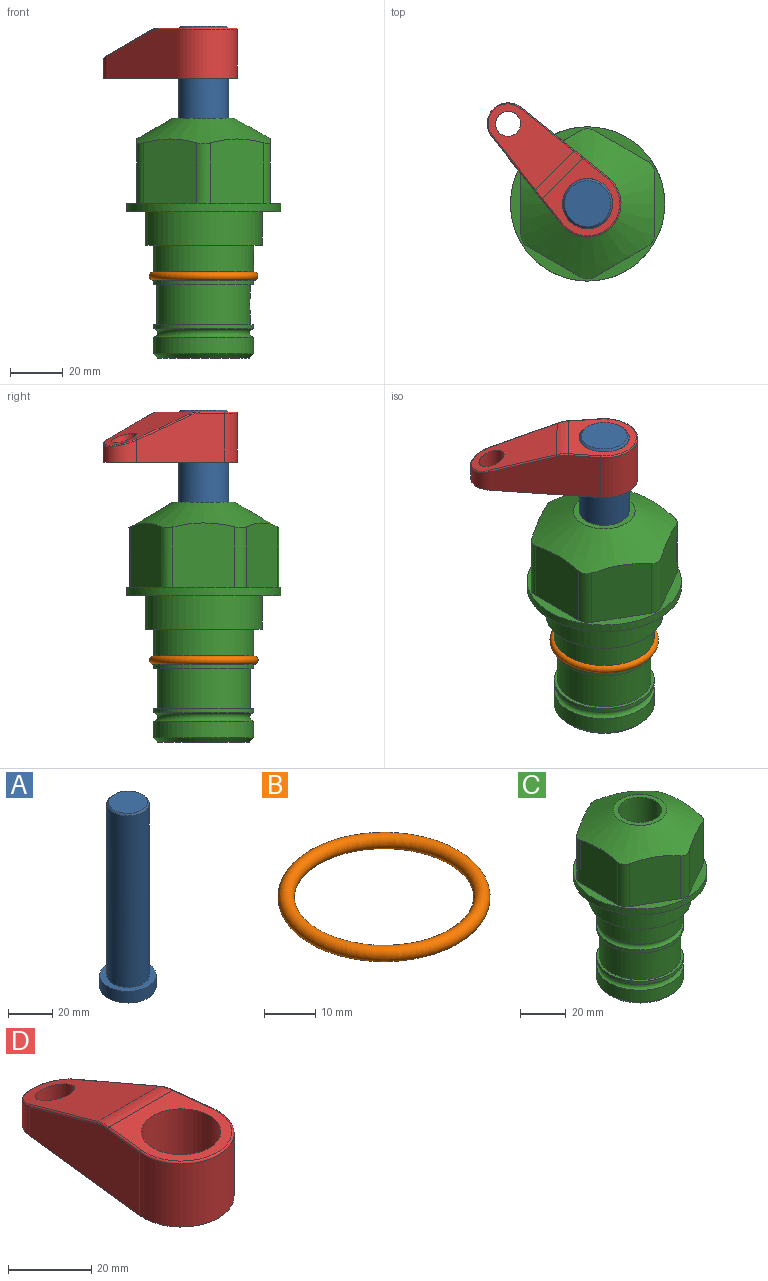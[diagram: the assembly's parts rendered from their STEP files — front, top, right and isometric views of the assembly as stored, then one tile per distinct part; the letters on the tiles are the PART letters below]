
ASSEMBLY  parts=4 mates=2
PART A: 6 faces, bbox 25.4x25.4x101.6 mm
  f0: plane 17.46x17.46mm, normal (0,0,1), area 239.5mm2, adj f5
  f1: plane 25.4x25.4mm, normal (0,0,-1), area 506.7mm2, adj f2
  f2: cylinder r=12.7mm len=25.4mm, axis (0,0,1), area 506.7mm2, adj f1,f3
  f3: plane 25.4x25.4mm, normal (0,0,1), area 221.7mm2, adj f2,f4
  f4: cylinder r=9.53mm len=94.46mm, axis (0,0,1), area 5653mm2, adj f3,f5
  f5: cone r=8.73mm half-angle=45deg, axis (0,0,-1), area 64.4mm2, adj f0,f4
PART B: 1 faces, bbox 44.7x44.7x3.2 mm
  f0: torus R=19.05mm, axis (0,0,1), area 1193.9mm2
PART C: 36 faces, bbox 58.7x58.7x91.2 mm
  f0: cylinder r=17.78mm len=35.56mm, axis (0,0,1), area 1670.8mm2, adj f23,f24,f31
  f1: cylinder r=19.05mm len=38.1mm, axis (0,0,1), area 1191.9mm2, adj f26,f27,f30
  f2: plane 58.66x58.66mm, normal (0,0,-1), area 1150.6mm2, adj f3,f28
  f3: cylinder r=29.33mm len=58.66mm, axis (0,0,-1), area 585.1mm2, adj f2,f4
  f4: plane 58.66x58.66mm, normal (0,0,1), area 475.9mm2, adj f3,f5,f6,f7,f8,f9,f10,f11
  f5: plane 24.5x20.32mm, normal (-0.5,0.87,0), area 562.8mm2, adj f4,f15,f16,f17
  f6: plane 24.5x20.32mm, normal (0.5,0.87,0), area 562.8mm2, adj f4,f14,f15,f17
  f7: plane 24.5x23.48mm, normal (1,0,0), area 562.8mm2, adj f4,f13,f14,f17
  f8: plane 24.5x20.32mm, normal (0.5,-0.87,0), area 562.8mm2, adj f4,f12,f13,f17
  f9: plane 24.5x20.32mm, normal (-0.5,-0.87,0), area 562.8mm2, adj f4,f11,f12,f17
  f10: plane 24.5x23.48mm, normal (-1,0,0), area 562.8mm2, adj f4,f11,f16,f17
  f11: cylinder r=5.08mm len=23.01mm, axis (0,0,-1), area 121.2mm2, adj f4,f9,f10,f17
  f12: cylinder r=5.08mm len=23.01mm, axis (0,0,-1), area 121.2mm2, adj f4,f8,f9,f17
  f13: cylinder r=5.08mm len=23.01mm, axis (0,0,-1), area 121.2mm2, adj f4,f7,f8,f17
  f14: cylinder r=5.08mm len=23.01mm, axis (0,0,-1), area 121.2mm2, adj f4,f6,f7,f17
  f15: cylinder r=5.08mm len=23.01mm, axis (0,0,-1), area 121.2mm2, adj f4,f5,f6,f17
  f16: cylinder r=5.08mm len=23.01mm, axis (0,0,-1), area 121.2mm2, adj f4,f5,f10,f17
  f17: cone r=11.73mm half-angle=60deg, axis (0,0,-1), area 2071.8mm2, adj f5,f6,f7,f8,f9,f10,f11,f12
  f18: plane 23.46x23.46mm, normal (0,0,1), area 147.4mm2, adj f17,f35
  f19: plane 34.93x34.93mm, normal (0,0,-1), area 958mm2, adj f29
  f20: cylinder r=19.05mm len=38.1mm, axis (0,0,1), area 760.1mm2, adj f21,f29
  f21: torus R=19.05mm, axis (0,0,1), area 565.3mm2, adj f20,f22
  f22: cylinder r=19.05mm len=38.1mm, axis (0,0,1), area 190mm2, adj f21,f23
  f23: plane 38.1x38.1mm, normal (0,0,1), area 146.9mm2, adj f0,f22
  f24: plane 38.1x38.1mm, normal (0,0,-1), area 146.9mm2, adj f0,f25
  f25: cylinder r=19.05mm len=38.1mm, axis (0,0,1), area 190mm2, adj f24,f26
  f26: torus R=19.05mm, axis (0,0,1), area 565.3mm2, adj f1,f25
  f27: plane 44.45x44.45mm, normal (0,0,-1), area 411.7mm2, adj f1,f28
  f28: cylinder r=22.23mm len=44.45mm, axis (0,0,1), area 1773.5mm2, adj f2,f27
  f29: cone r=19.05mm half-angle=45deg, axis (0,0,1), area 257.5mm2, adj f19,f20
  f30: cylinder r=3.17mm len=6.75mm, axis (-1,0,0), area 128mm2, adj f1,f33
  f31: cylinder r=3.17mm len=6.35mm, axis (-1,0,0), area 102.5mm2, adj f0,f33
  f32: plane 25.4x25.4mm, normal (0,0,1), area 506.7mm2, adj f33
  f33: cylinder r=12.7mm len=66.42mm, axis (0,0,-1), area 5236.2mm2, adj f30,f31,f32,f34
  f34: cone r=9.53mm half-angle=30deg, axis (0,0,-1), area 443.4mm2, adj f33,f35
  f35: cylinder r=9.53mm len=19.05mm, axis (0,0,-1), area 849mm2, adj f18,f34
PART D: 44 faces, bbox 27.5x64.5x19.1 mm
  f0: plane 2.3x0.95mm, normal (0,0,-1), area 1mm2, adj f25,f30,f34
  f1: plane 63.5x25.4mm, normal (0,0,-1), area 561.7mm2, adj f2,f3,f4,f5,f6,f7,f19,f20
  f2: cylinder r=12.7mm len=25.4mm, axis (0,0,-1), area 792.2mm2, adj f1,f3,f5,f13
  f3: plane 42.33x18.54mm, normal (0.99,0.11,0), area 647mm2, adj f1,f2,f4,f11,f12,f14
  f4: cylinder r=7.94mm len=15.78mm, axis (0,0,-1), area 158.6mm2, adj f1,f3,f5,f16
  f5: plane 42.33x18.54mm, normal (-0.99,0.11,0), area 647mm2, adj f1,f2,f4,f15,f17,f18
  f6: cylinder r=9.53mm len=19.05mm, axis (0,0,-1), area 1140.1mm2, adj f1,f8
  f7: cylinder r=4.76mm len=10.98mm, axis (0,0,-1), area 276.1mm2, adj f1,f9
  f8: plane 25.83x24.38mm, normal (0,0,1), area 262.2mm2, adj f6,f10,f11,f13,f15
  f9: plane 32.49x20.55mm, normal (0,0.34,0.94), area 489.9mm2, adj f7,f10,f14,f16,f18
  f10: cylinder r=12.7mm len=21.49mm, axis (-1,0,0), area 93.2mm2, adj f8,f9,f12,f17
  f11: cylinder r=0.51mm len=12.34mm, axis (0.11,-0.99,0), area 9.9mm2, adj f3,f8,f12,f13
  f12: bspline ~7.62x1.64mm, area 3.5mm2, adj f3,f10,f11,f14
  f13: torus R=12.19mm, axis (0,0,1), area 33.6mm2, adj f2,f8,f11,f15
  f14: cylinder r=0.51mm len=26.01mm, axis (0.1,-0.93,0.34), area 21.6mm2, adj f3,f9,f12,f16
  f15: cylinder r=0.51mm len=12.34mm, axis (0.11,0.99,0), area 9.9mm2, adj f5,f8,f13,f17
  f16: bspline ~15.78x7.05mm, area 15.7mm2, adj f4,f9,f14,f18
  f17: bspline ~7.62x1.64mm, area 3.5mm2, adj f5,f10,f15,f18
  f18: cylinder r=0.51mm len=26.01mm, axis (0.1,0.93,-0.34), area 21.6mm2, adj f5,f9,f16,f17
  f19: plane 21.6x14.29mm, normal (-0.99,-0.11,0), area 242.6mm2, adj f1,f26,f28,f34,f36,f38
  f20: plane 21.6x14.29mm, normal (0.99,-0.11,0), area 242.6mm2, adj f1,f27,f29,f37,f39,f41
  f21: cylinder r=12.7mm len=14.29mm, axis (0,0,-1), area 173.2mm2, adj f1,f26,f27,f30,f31,f33
  f22: cylinder r=7.94mm len=7.63mm, axis (0,0,-1), area 53.8mm2, adj f1,f28,f29,f42
  f23: plane 2.3x0.95mm, normal (0,0,-1), area 1mm2, adj f25,f33,f37
  f24: plane 17.94x12.32mm, normal (0,-0.34,-0.94), area 191.2mm2, adj f25,f38,f41,f42
  f25: cylinder r=9.53mm len=12.93mm, axis (-1,0,0), area 37.5mm2, adj f0,f23,f24,f31,f36,f39
  f26: cylinder r=1.59mm len=14.29mm, axis (0,0,-1), area 49mm2, adj f1,f19,f21,f32
  f27: cylinder r=1.59mm len=14.29mm, axis (0,0,-1), area 49mm2, adj f1,f20,f21,f35
  f28: cylinder r=1.59mm len=7.28mm, axis (0,0,-1), area 22.1mm2, adj f1,f19,f22,f40
  f29: cylinder r=1.59mm len=7.28mm, axis (0,0,-1), area 22.1mm2, adj f1,f20,f22,f43
  f30: torus R=14.29mm, axis (0,0,1), area 5.8mm2, adj f0,f21,f31,f32
  f31: bspline ~11.06x2.73mm, area 20.8mm2, adj f21,f25,f30,f33
  f32: sphere r=1.59mm, area 5.4mm2, adj f26,f30,f34
  f33: torus R=14.29mm, axis (0,0,1), area 5.8mm2, adj f21,f23,f31,f35
  f34: cylinder r=1.59mm len=1.68mm, axis (-0.11,0.99,0), area 2.4mm2, adj f0,f19,f32,f36
  f35: sphere r=1.59mm, area 5.4mm2, adj f27,f33,f37
  f36: bspline ~5.82x2.33mm, area 7.7mm2, adj f19,f25,f34,f38
  f37: cylinder r=1.59mm len=1.68mm, axis (0.11,0.99,0), area 2.4mm2, adj f20,f23,f35,f39
  f38: cylinder r=1.59mm len=18.33mm, axis (0.1,-0.93,0.34), area 46.7mm2, adj f19,f24,f36,f40
  f39: bspline ~5.82x2.33mm, area 7.7mm2, adj f20,f25,f37,f41
  f40: sphere r=1.59mm, area 3.6mm2, adj f28,f38,f42
  f41: cylinder r=1.59mm len=18.33mm, axis (0.1,0.93,-0.34), area 46.7mm2, adj f20,f24,f39,f43
  f42: bspline ~8.31x1.84mm, area 15.3mm2, adj f22,f24,f40,f43
  f43: sphere r=1.59mm, area 3.6mm2, adj f29,f41,f42
PLACE A rot(axis=(0,0,1),44.9deg) t=(0,0,-3.06)mm
PLACE B at identity
PLACE C at identity fixed
PLACE D rot(axis=(0,0,1),44.9deg) t=(0,0,50.76)mm
MATE fastened D.f2 <-> A.f2  axis (0,0,-1) through (0,0,69.81)mm
MATE cylindrical A.f2 <-> C.f0  axis (0,0,1) through (0,0,22.58)mm
